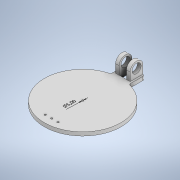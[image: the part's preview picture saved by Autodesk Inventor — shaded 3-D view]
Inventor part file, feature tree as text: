
AUTODESK INVENTOR PART (.ipt)
format: ipt  version: 2021 (Build 250183000, 183)  size: 376,832 bytes
history: native  units: mm
features: extrude x25, sketch x25, other x2, thicken_offset x2, fillet x2
ambient origin geometry x8: Origin, YZ Plane, XZ Plane, XY Plane, X Axis, Y Axis, Z Axis, Center Point
bodies: Solid1 (feature_tree)
feature tree (56):
  other  "Annotations"
  extrude  "Extrusion1"  Depth=10.0mm TaperAngle=0.0deg
  extrude  "Extrusion2"  Depth=20.0mm
  extrude  "Extrusion3"  Depth=17.5mm
  extrude  "Extrusion4"  Depth=5.0mm
  extrude  "Extrusion5"  Depth=10.0mm TaperAngle=0.0deg
  extrude  "Extrusion6"  Depth=10.0mm TaperAngle=0.0deg
  extrude  "Extrusion7"  Depth=15.0mm
  extrude  "Extrusion8"  Depth=30.0mm
  thicken_offset  "Thicken1"
  thicken_offset  "Thicken2"
  extrude  "Extrusion9"  Depth=15.0mm
  sketch  "Sketch11"  dims[d26=30.0mm d27=0.0mm d28=25.0mm]
  extrude  "Extrusion10"  Depth=30.0mm
  extrude  "Extrusion11"  Depth=15.0mm
  extrude  "Extrusion12"  Depth=30.0mm TaperAngle=0.0deg
  extrude  "Extrusion13"  Depth=15.0mm TaperAngle=0.0deg
  extrude  "Extrusion14"  Depth=15.0mm
  extrude  "Extrusion15"  Depth=10.0mm
  extrude  "Extrusion17"  Depth=10.0mm
  extrude  "Extrusion18"  Depth=35.0mm
  extrude  "Extrusion19"  Depth=5.0mm
  extrude  "Extrusion20"  Depth=5.0mm
  extrude  "Extrusion27"  Depth=5.0mm
  extrude  "Extrusion28"  Depth=40.0mm TaperAngle=0.0deg
  extrude  "Extrusion29"  Depth=35.0mm
  fillet  "Fillet4"  Radius=40.0mm
  extrude  "Extrusion30"  Depth=40.0mm TaperAngle=0.0deg
  extrude  "Extrusion31"  Depth=20.0mm
  fillet  "Fillet5"  Radius=150.0mm
  extrude  "Extrusion32"  Depth=5.0mm
  sketch  "Sketch1"  dims[d0=210.0mm d1=10.0mm d2=0.0mm]
  sketch  "Sketch2"  dims[d4=80.0mm d5=20.0mm]
  sketch  "Sketch3"  dims[d6=17.5mm d7=17.5mm]
  sketch  "Sketch4"  dims[d8=5.0mm d9=5.0mm]
  sketch  "Sketch5"  dims[d10=5.0mm d11=10.0mm d12=0.0mm]
  sketch  "Sketch6"  dims[d13=5.0mm d14=10.0mm d15=0.0mm]
  sketch  "Sketch7"  dims[d20=15.0mm d21=15.0mm]
  sketch  "Sketch8"  dims[d22=30.0mm d23=30.0mm]
  sketch  "Sketch10"  dims[d24=7.5mm d25=15.0mm]
  sketch  "Sketch12"  dims[d29=15.0mm d30=15.0mm]
  sketch  "Sketch13"  dims[d31=180.0deg d32=30.0mm d33=0.0mm]
  sketch  "Sketch14"  dims[d34=10.0mm d35=15.0mm d36=0.0mm]
  sketch  "Sketch15"  dims[d37=15.0mm d38=0.0mm d42=100.0mm]
  sketch  "Sketch16"  dims[d43=10.0mm d44=10.0mm]
  sketch  "Sketch18"  dims[d45=35.0mm d46=10.0mm]
  sketch  "Sketch19"  dims[d47=10.0mm d48=35.0mm]
  sketch  "Sketch20"  dims[d49=35.0mm d50=0.0mm d56=5.0mm]
  sketch  "Sketch21"  dims[d57=5.0mm d58=5.0mm]
  sketch  "Sketch28"  dims[d59=5.0mm d60=22.5mm]
  sketch  "Sketch29"  dims[d61=25.0mm d62=40.0mm d63=0.0mm]
  sketch  "Sketch30"  dims[d73=35.0mm d74=35.0mm d75=40.0mm d78=35.0mm]
  sketch  "Sketch31"  dims[d79=40.0mm d80=0.0mm d81=40.0mm d82=0.0mm]
  sketch  "Sketch32"  dims[d83=10.0mm d84=20.0mm d85=150.0mm d86=0.0mm]
  sketch  "Sketch33"  dims[d87=150.0mm d88=0.0mm d89=100.0mm d90=20.0mm d91=35.0mm d92=10.0mm d93=20.0mm d94=10.0mm d95=35.0mm d96=10.0mm d97=40.0mm d98=0.0mm d99=17.5mm d100=25.0mm d101=40.0mm d102=0.0mm d117=40.0mm d118=0.0mm d119=85.0mm d120=5.0mm d121=5.0mm d122=5.0mm d123=10.0mm d124=0.0mm d125=5.0mm d126=5.0mm d127=5.0mm d128=10.0mm d129=0.0mm d130=10.0mm d131=0.0mm d165=145.0mm d166=25.0mm d167=10.0mm d168=0.0mm d169=40.0mm d170=0.0mm d173=10.0mm d174=10.0mm d175=35.0mm d176=10.0mm d177=10.0mm d178=10.0mm d179=40.0mm d180=0.0mm d181=17.5mm d182=25.0mm d183=25.0mm d184=210.0mm d185=40.0mm d186=0.0mm d187=25.0mm d188=40.0mm d189=0.0mm d190=5.0mm d191=20.0mm d192=35.0mm d193=40.0mm d194=0.0mm d16=46.771507mm d17=5.0mm]
  other  "Diameter Dimension 1"
